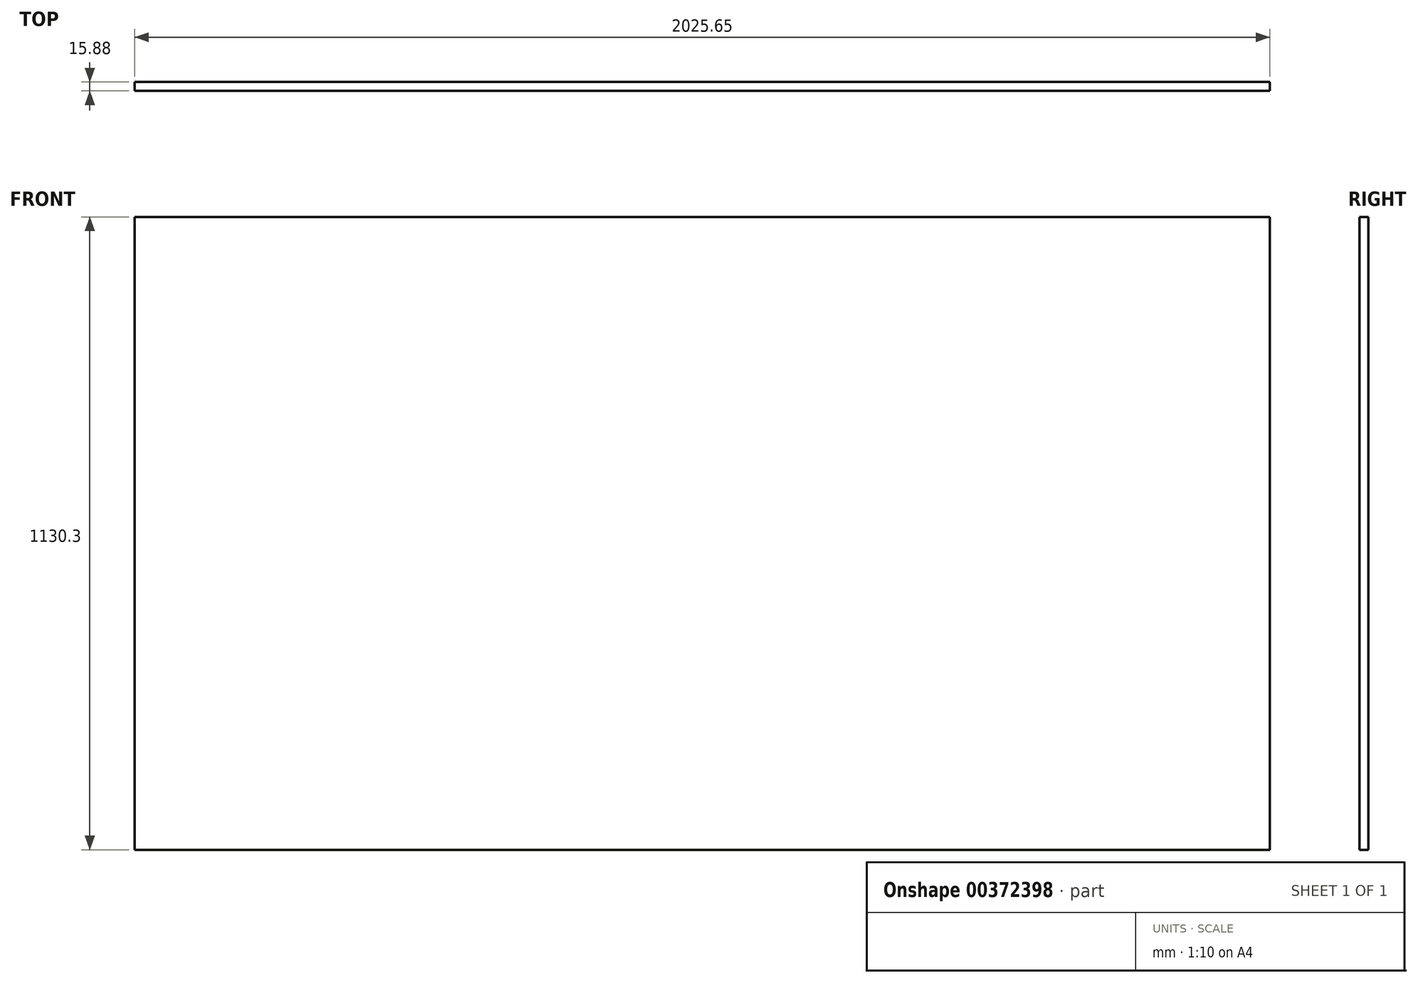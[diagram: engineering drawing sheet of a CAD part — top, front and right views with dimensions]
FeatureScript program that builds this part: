
annotation { "Feature Type Name" : "Feature", "Feature Type Description" : "" }
export const myFeature = defineFeature(function(context is Context, id is Id, definition is map)
    precondition{}
    {
        {
            var Q0;
            Q0=qCreatedBy(makeId("Front.planeOp"),FACE);
            var sketch = newSketch(context, id + "F0", { "sketchPlane" : qUnion([Q0])});
            skLineSegment(sketch, "E0.bottom", {"start": v(1104.9, -565.15) * mm, "end": v(-920.75, -565.15) * mm});
            skLineSegment(sketch, "E0.top", {"start": v(1104.9, 565.15) * mm, "end": v(-920.75, 565.15) * mm});
            skLineSegment(sketch, "E0.left", {"start": v(1104.9, -565.15) * mm, "end": v(1104.9, 565.15) * mm});
            skPoint(sketch, "E0.middle", {"position": v(0, 0) * mm});
            skPoint(sketch, "E1.orphan", {"position": v(-1104.9, -565.15) * mm});
            skLineSegment(sketch, "E2", {"start": v(-920.75, -565.15) * mm, "end": v(-920.75, 565.15) * mm});
            skPoint(sketch, "E3.start.orphan", {"position": v(-1104.9, 565.15) * mm});
            skSolve(sketch);
        }
        {
            var Q0;
            Q0=qSketchRegion(id+"F0",true);
            extrude(context, id + "F1", {"entities" : qUnion([Q0]), "depth" : 15.88 * mm});
        }
    });
